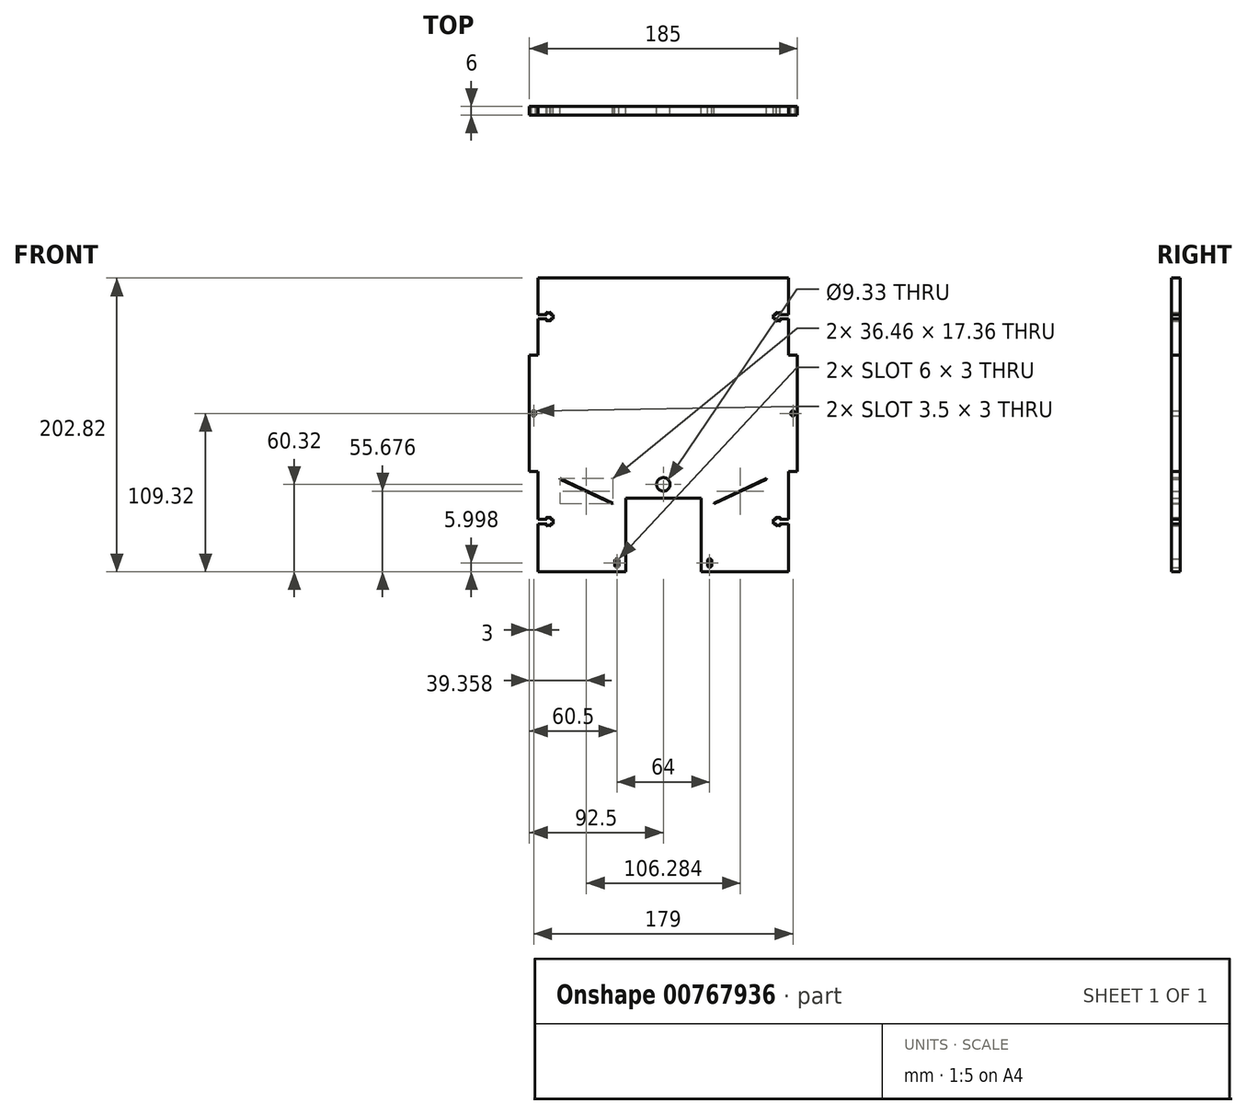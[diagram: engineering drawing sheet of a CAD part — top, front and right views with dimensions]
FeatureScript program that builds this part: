
annotation { "Feature Type Name" : "Feature", "Feature Type Description" : "" }
export const myFeature = defineFeature(function(context is Context, id is Id, definition is map)
    precondition{}
    {
        {
            var Q0;
            Q0=qCreatedBy(makeId("Front.planeOp"),FACE);
            var sketch = newSketch(context, id + "F0", { "sketchPlane" : qUnion([Q0])});
            skLineSegment(sketch, "E0.top", {"start": v(13.5, 187) * mm, "end": v(186.5, 187) * mm});
            skLineSegment(sketch, "E1", {"start": v(186.5, 187) * mm, "end": v(186.5, 161.75) * mm});
            skLineSegment(sketch, "E2.MirrorCS", {"start": v(13.5, 187) * mm, "end": v(13.5, 161.75) * mm});
            skLineSegment(sketch, "E3", {"start": v(100, 187) * mm, "end": v(100, -11.94) * mm, "construction": true});
            skLineSegment(sketch, "E4", {"start": v(74, 0) * mm, "end": v(74, 35) * mm});
            skLineSegment(sketch, "E5", {"start": v(126, 0) * mm, "end": v(126, 35) * mm});
            skLineSegment(sketch, "E6", {"start": v(74, 35) * mm, "end": v(126, 35) * mm});
            skLineSegment(sketch, "E7", {"start": v(-16.45, 22) * mm, "end": v(92.36, 22) * mm, "construction": true});
            skLineSegment(sketch, "E8", {"start": v(80, 24.12) * mm, "end": v(13.5, 55.14) * mm, "construction": true});
            skLineSegment(sketch, "E9.0", {"start": v(80.22, 24.58) * mm, "end": v(13.71, 55.59) * mm, "construction": true});
            skLineSegment(sketch, "E10", {"start": v(46.96, 40.08) * mm, "end": v(46.75, 39.63) * mm, "construction": true});
            skLineSegment(sketch, "E11.0", {"start": v(28.84, 48.53) * mm, "end": v(28.63, 48.08) * mm});
            skLineSegment(sketch, "E12.0", {"start": v(65.09, 31.63) * mm, "end": v(64.88, 31.18) * mm});
            skLineSegment(sketch, "E13", {"start": v(65.09, 31.63) * mm, "end": v(28.84, 48.53) * mm});
            skLineSegment(sketch, "E14", {"start": v(28.63, 48.08) * mm, "end": v(64.88, 31.18) * mm});
            skLineSegment(sketch, "E15", {"start": v(80, 24.12) * mm, "end": v(80.22, 24.58) * mm, "construction": true});
            skLineSegment(sketch, "E16", {"start": v(13.5, 55.14) * mm, "end": v(13.71, 55.59) * mm, "construction": true});
            skLineSegment(sketch, "E17.MirrorCS", {"start": v(134.91, 31.63) * mm, "end": v(171.16, 48.53) * mm});
            skLineSegment(sketch, "E18.MirrorCS", {"start": v(171.37, 48.08) * mm, "end": v(135.12, 31.18) * mm});
            skLineSegment(sketch, "E19.MirrorCS", {"start": v(134.91, 31.63) * mm, "end": v(135.12, 31.18) * mm});
            skLineSegment(sketch, "E20.MirrorCS", {"start": v(171.16, 48.53) * mm, "end": v(171.37, 48.08) * mm});
            skCircle(sketch, "E21", {"center": v(100, 44.5) * mm, "radius": 4.67 * mm});
            skLineSegment(sketch, "E22", {"start": v(74, 0) * mm, "end": v(74, -15.82) * mm});
            skLineSegment(sketch, "E23", {"start": v(74, -15.82) * mm, "end": v(13.5, -15.82) * mm});
            skLineSegment(sketch, "E24.MirrorCS", {"start": v(126, -15.82) * mm, "end": v(186.5, -15.82) * mm});
            skLineSegment(sketch, "E25.MirrorCS", {"start": v(126, 0) * mm, "end": v(126, -15.82) * mm});
            skLineSegment(sketch, "E26.left", {"start": v(66.5, -8.32) * mm, "end": v(66.5, -11.32) * mm});
            skLineSegment(sketch, "E26.right", {"start": v(69.5, -8.32) * mm, "end": v(69.5, -11.32) * mm});
            skArc(sketch, "E27", {"start": v(69.5, -8.32) * mm, "mid": v(68, -6.82) * mm, "end": v(66.5, -8.32) * mm});
            skArc(sketch, "E28", {"start": v(66.5, -11.32) * mm, "mid": v(68, -12.82) * mm, "end": v(69.5, -11.32) * mm});
            skArc(sketch, "E29.MirrorCS", {"start": v(130.5, -8.32) * mm, "mid": v(132, -6.82) * mm, "end": v(133.5, -8.32) * mm});
            skLineSegment(sketch, "E30.MirrorCS", {"start": v(130.5, -8.32) * mm, "end": v(130.5, -11.32) * mm});
            skLineSegment(sketch, "E31.MirrorCS", {"start": v(133.5, -8.32) * mm, "end": v(133.5, -11.32) * mm});
            skArc(sketch, "E32.MirrorCS", {"start": v(133.5, -11.32) * mm, "mid": v(132, -12.82) * mm, "end": v(130.5, -11.32) * mm});
            skLineSegment(sketch, "E33", {"start": v(7.5, 133.5) * mm, "end": v(7.5, 53.5) * mm});
            skLineSegment(sketch, "E34.MirrorCS", {"start": v(192.5, 133.5) * mm, "end": v(192.5, 53.5) * mm});
            skPoint(sketch, "E35", {"position": v(13.5, 160.25) * mm});
            skPoint(sketch, "E36", {"position": v(186.5, 160.25) * mm});
            skLineSegment(sketch, "E37", {"start": v(13.5, 53.4) * mm, "end": v(13.5, 20.34) * mm});
            skLineSegment(sketch, "E38", {"start": v(186.5, 53.4) * mm, "end": v(186.5, 20.34) * mm});
            skPoint(sketch, "E39", {"position": v(13.5, 18.84) * mm});
            skPoint(sketch, "E40", {"position": v(186.5, 18.84) * mm});
            skLineSegment(sketch, "E41.bottom", {"start": v(19.2, 158.75) * mm, "end": v(13.5, 158.75) * mm});
            skLineSegment(sketch, "E41.top", {"start": v(19.2, 161.75) * mm, "end": v(13.5, 161.75) * mm});
            skLineSegment(sketch, "E42", {"start": v(19.5, 158.45) * mm, "end": v(19.5, 157.7) * mm});
            skLineSegment(sketch, "E43", {"start": v(19.7, 157.5) * mm, "end": v(21.8, 157.5) * mm});
            skLineSegment(sketch, "E44", {"start": v(22, 157.7) * mm, "end": v(22, 158.45) * mm});
            skLineSegment(sketch, "E45.MirrorCS", {"start": v(19.5, 162.05) * mm, "end": v(19.5, 162.8) * mm});
            skLineSegment(sketch, "E46.MirrorCS", {"start": v(19.7, 163) * mm, "end": v(21.8, 163) * mm});
            skLineSegment(sketch, "E47.MirrorCS", {"start": v(22, 162.8) * mm, "end": v(22, 162.05) * mm});
            skPoint(sketch, "E48.visualSharp", {"position": v(19.5, 161.75) * mm});
            skArc(sketch, "E48.filletArc", {"start": v(19.2, 161.75) * mm, "mid": v(19.41, 161.84) * mm, "end": v(19.5, 162.05) * mm});
            skPoint(sketch, "E49.visualSharp", {"position": v(19.5, 158.75) * mm});
            skArc(sketch, "E49.filletArc", {"start": v(19.5, 158.45) * mm, "mid": v(19.41, 158.66) * mm, "end": v(19.2, 158.75) * mm});
            skPoint(sketch, "E50.visualSharp", {"position": v(22, 158.75) * mm});
            skArc(sketch, "E50.filletArc", {"start": v(22.3, 158.75) * mm, "mid": v(22.09, 158.66) * mm, "end": v(22, 158.45) * mm});
            skPoint(sketch, "E51.visualSharp", {"position": v(22, 161.75) * mm});
            skArc(sketch, "E51.filletArc", {"start": v(22, 162.05) * mm, "mid": v(22.09, 161.84) * mm, "end": v(22.3, 161.75) * mm});
            skArc(sketch, "E52", {"start": v(19.7, 157.5) * mm, "mid": v(19.36, 157.36) * mm, "end": v(19.5, 157.7) * mm});
            skArc(sketch, "E53", {"start": v(21.8, 157.5) * mm, "mid": v(22.14, 157.36) * mm, "end": v(22, 157.7) * mm});
            skArc(sketch, "E54", {"start": v(22, 162.8) * mm, "mid": v(22.14, 163.14) * mm, "end": v(21.8, 163) * mm});
            skArc(sketch, "E55", {"start": v(19.5, 162.8) * mm, "mid": v(19.36, 163.14) * mm, "end": v(19.7, 163) * mm});
            skLineSegment(sketch, "E56", {"start": v(24, 158.75) * mm, "end": v(24, 161.75) * mm});
            skLineSegment(sketch, "E57", {"start": v(24, 158.75) * mm, "end": v(22.3, 158.75) * mm});
            skLineSegment(sketch, "E58", {"start": v(24, 161.75) * mm, "end": v(22.3, 161.75) * mm});
            skLineSegment(sketch, "E59.bottom", {"start": v(19.2, 17.34) * mm, "end": v(13.5, 17.34) * mm});
            skLineSegment(sketch, "E59.top", {"start": v(19.2, 20.34) * mm, "end": v(13.5, 20.34) * mm});
            skLineSegment(sketch, "E60", {"start": v(19.5, 17.04) * mm, "end": v(19.5, 16.29) * mm});
            skLineSegment(sketch, "E61", {"start": v(19.7, 16.09) * mm, "end": v(21.8, 16.09) * mm});
            skLineSegment(sketch, "E62", {"start": v(22, 16.29) * mm, "end": v(22, 17.04) * mm});
            skLineSegment(sketch, "E63.MirrorCS", {"start": v(19.5, 20.64) * mm, "end": v(19.5, 21.39) * mm});
            skLineSegment(sketch, "E64.MirrorCS", {"start": v(19.7, 21.59) * mm, "end": v(21.8, 21.59) * mm});
            skLineSegment(sketch, "E65.MirrorCS", {"start": v(22, 21.39) * mm, "end": v(22, 20.64) * mm});
            skPoint(sketch, "E66.visualSharp", {"position": v(19.5, 20.34) * mm});
            skArc(sketch, "E66.filletArc", {"start": v(19.2, 20.34) * mm, "mid": v(19.41, 20.43) * mm, "end": v(19.5, 20.64) * mm});
            skPoint(sketch, "E67.visualSharp", {"position": v(19.5, 17.34) * mm});
            skArc(sketch, "E67.filletArc", {"start": v(19.5, 17.04) * mm, "mid": v(19.41, 17.25) * mm, "end": v(19.2, 17.34) * mm});
            skPoint(sketch, "E68.visualSharp", {"position": v(22, 17.34) * mm});
            skArc(sketch, "E68.filletArc", {"start": v(22.3, 17.34) * mm, "mid": v(22.09, 17.25) * mm, "end": v(22, 17.04) * mm});
            skPoint(sketch, "E69.visualSharp", {"position": v(22, 20.34) * mm});
            skArc(sketch, "E69.filletArc", {"start": v(22, 20.64) * mm, "mid": v(22.09, 20.43) * mm, "end": v(22.3, 20.34) * mm});
            skArc(sketch, "E70", {"start": v(19.7, 16.09) * mm, "mid": v(19.36, 15.95) * mm, "end": v(19.5, 16.29) * mm});
            skArc(sketch, "E71", {"start": v(21.8, 16.09) * mm, "mid": v(22.14, 15.95) * mm, "end": v(22, 16.29) * mm});
            skArc(sketch, "E72", {"start": v(22, 21.39) * mm, "mid": v(22.14, 21.73) * mm, "end": v(21.8, 21.59) * mm});
            skArc(sketch, "E73", {"start": v(19.5, 21.39) * mm, "mid": v(19.36, 21.73) * mm, "end": v(19.7, 21.59) * mm});
            skLineSegment(sketch, "E74", {"start": v(24, 17.34) * mm, "end": v(24, 20.34) * mm});
            skLineSegment(sketch, "E75", {"start": v(24, 17.34) * mm, "end": v(22.3, 17.34) * mm});
            skLineSegment(sketch, "E76", {"start": v(24, 20.34) * mm, "end": v(22.3, 20.34) * mm});
            skLineSegment(sketch, "E77.bottom", {"start": v(180.8, 161.75) * mm, "end": v(186.5, 161.75) * mm});
            skLineSegment(sketch, "E77.top", {"start": v(180.8, 158.75) * mm, "end": v(186.5, 158.75) * mm});
            skLineSegment(sketch, "E78", {"start": v(180.5, 162.05) * mm, "end": v(180.5, 162.8) * mm});
            skLineSegment(sketch, "E79", {"start": v(180.3, 163) * mm, "end": v(178.2, 163) * mm});
            skLineSegment(sketch, "E80", {"start": v(178, 162.8) * mm, "end": v(178, 162.05) * mm});
            skLineSegment(sketch, "E81.MirrorCS", {"start": v(180.5, 158.45) * mm, "end": v(180.5, 157.7) * mm});
            skLineSegment(sketch, "E82.MirrorCS", {"start": v(180.3, 157.5) * mm, "end": v(178.2, 157.5) * mm});
            skLineSegment(sketch, "E83.MirrorCS", {"start": v(178, 157.7) * mm, "end": v(178, 158.45) * mm});
            skPoint(sketch, "E84.visualSharp", {"position": v(180.5, 158.75) * mm});
            skArc(sketch, "E84.filletArc", {"start": v(180.8, 158.75) * mm, "mid": v(180.59, 158.66) * mm, "end": v(180.5, 158.45) * mm});
            skPoint(sketch, "E85.visualSharp", {"position": v(180.5, 161.75) * mm});
            skArc(sketch, "E85.filletArc", {"start": v(180.5, 162.05) * mm, "mid": v(180.59, 161.84) * mm, "end": v(180.8, 161.75) * mm});
            skPoint(sketch, "E86.visualSharp", {"position": v(178, 161.75) * mm});
            skArc(sketch, "E86.filletArc", {"start": v(177.7, 161.75) * mm, "mid": v(177.91, 161.84) * mm, "end": v(178, 162.05) * mm});
            skPoint(sketch, "E87.visualSharp", {"position": v(178, 158.75) * mm});
            skArc(sketch, "E87.filletArc", {"start": v(178, 158.45) * mm, "mid": v(177.91, 158.66) * mm, "end": v(177.7, 158.75) * mm});
            skArc(sketch, "E88", {"start": v(180.3, 163) * mm, "mid": v(180.64, 163.14) * mm, "end": v(180.5, 162.8) * mm});
            skArc(sketch, "E89", {"start": v(178.2, 163) * mm, "mid": v(177.86, 163.14) * mm, "end": v(178, 162.8) * mm});
            skArc(sketch, "E90", {"start": v(178, 157.7) * mm, "mid": v(177.86, 157.36) * mm, "end": v(178.2, 157.5) * mm});
            skArc(sketch, "E91", {"start": v(180.5, 157.7) * mm, "mid": v(180.64, 157.36) * mm, "end": v(180.3, 157.5) * mm});
            skLineSegment(sketch, "E92", {"start": v(176, 161.75) * mm, "end": v(176, 158.75) * mm});
            skLineSegment(sketch, "E93", {"start": v(176, 161.75) * mm, "end": v(177.7, 161.75) * mm});
            skLineSegment(sketch, "E94", {"start": v(176, 158.75) * mm, "end": v(177.7, 158.75) * mm});
            skLineSegment(sketch, "E95.bottom", {"start": v(180.8, 20.34) * mm, "end": v(186.5, 20.34) * mm});
            skLineSegment(sketch, "E95.top", {"start": v(180.8, 17.34) * mm, "end": v(186.5, 17.34) * mm});
            skLineSegment(sketch, "E96", {"start": v(180.5, 20.64) * mm, "end": v(180.5, 21.39) * mm});
            skLineSegment(sketch, "E97", {"start": v(180.3, 21.59) * mm, "end": v(178.2, 21.59) * mm});
            skLineSegment(sketch, "E98", {"start": v(178, 21.39) * mm, "end": v(178, 20.64) * mm});
            skLineSegment(sketch, "E99.MirrorCS", {"start": v(180.5, 17.04) * mm, "end": v(180.5, 16.29) * mm});
            skLineSegment(sketch, "E100.MirrorCS", {"start": v(180.3, 16.09) * mm, "end": v(178.2, 16.09) * mm});
            skLineSegment(sketch, "E101.MirrorCS", {"start": v(178, 16.29) * mm, "end": v(178, 17.04) * mm});
            skPoint(sketch, "E102.visualSharp", {"position": v(180.5, 17.34) * mm});
            skArc(sketch, "E102.filletArc", {"start": v(180.8, 17.34) * mm, "mid": v(180.59, 17.25) * mm, "end": v(180.5, 17.04) * mm});
            skPoint(sketch, "E103.visualSharp", {"position": v(180.5, 20.34) * mm});
            skArc(sketch, "E103.filletArc", {"start": v(180.5, 20.64) * mm, "mid": v(180.59, 20.43) * mm, "end": v(180.8, 20.34) * mm});
            skPoint(sketch, "E104.visualSharp", {"position": v(178, 20.34) * mm});
            skArc(sketch, "E104.filletArc", {"start": v(177.7, 20.34) * mm, "mid": v(177.91, 20.43) * mm, "end": v(178, 20.64) * mm});
            skPoint(sketch, "E105.visualSharp", {"position": v(178, 17.34) * mm});
            skArc(sketch, "E105.filletArc", {"start": v(178, 17.04) * mm, "mid": v(177.91, 17.25) * mm, "end": v(177.7, 17.34) * mm});
            skArc(sketch, "E106", {"start": v(180.3, 21.59) * mm, "mid": v(180.64, 21.73) * mm, "end": v(180.5, 21.39) * mm});
            skArc(sketch, "E107", {"start": v(178.2, 21.59) * mm, "mid": v(177.86, 21.73) * mm, "end": v(178, 21.39) * mm});
            skArc(sketch, "E108", {"start": v(178, 16.29) * mm, "mid": v(177.86, 15.95) * mm, "end": v(178.2, 16.09) * mm});
            skArc(sketch, "E109", {"start": v(180.5, 16.29) * mm, "mid": v(180.64, 15.95) * mm, "end": v(180.3, 16.09) * mm});
            skLineSegment(sketch, "E110", {"start": v(176, 20.34) * mm, "end": v(176, 17.34) * mm});
            skLineSegment(sketch, "E111", {"start": v(176, 20.34) * mm, "end": v(177.7, 20.34) * mm});
            skLineSegment(sketch, "E112", {"start": v(176, 17.34) * mm, "end": v(177.7, 17.34) * mm});
            skLineSegment(sketch, "E113.trimOffspring", {"start": v(186.5, 17.34) * mm, "end": v(186.5, -15.82) * mm});
            skLineSegment(sketch, "E114.trimOffspring", {"start": v(13.5, 17.34) * mm, "end": v(13.5, -15.82) * mm});
            skLineSegment(sketch, "E115.trimOffspring", {"start": v(13.5, 158.75) * mm, "end": v(13.5, 133.6) * mm});
            skLineSegment(sketch, "E116.trimOffspring", {"start": v(186.5, 158.75) * mm, "end": v(186.5, 133.6) * mm});
            skLineSegment(sketch, "E117", {"start": v(7.5, 133.5) * mm, "end": v(7.5, 133.6) * mm});
            skLineSegment(sketch, "E118", {"start": v(7.5, 133.6) * mm, "end": v(13.5, 133.6) * mm});
            skLineSegment(sketch, "E119.MirrorCS", {"start": v(192.5, 133.6) * mm, "end": v(186.5, 133.6) * mm});
            skLineSegment(sketch, "E120.MirrorCS", {"start": v(192.5, 133.5) * mm, "end": v(192.5, 133.6) * mm});
            skPoint(sketch, "E121.MirrorCS.end.orphan", {"position": v(192.5, 133.5) * mm});
            skPoint(sketch, "E121.MirrorCS.start.orphan", {"position": v(186.5, 133.5) * mm});
            skLineSegment(sketch, "E122", {"start": v(192.5, 53.5) * mm, "end": v(192.5, 53.4) * mm});
            skLineSegment(sketch, "E123", {"start": v(192.5, 53.4) * mm, "end": v(186.5, 53.4) * mm});
            skPoint(sketch, "E124.MirrorCS.end.orphan", {"position": v(186.5, 53.5) * mm});
            skPoint(sketch, "E124.MirrorCS.start.orphan", {"position": v(192.5, 53.5) * mm});
            skLineSegment(sketch, "E125.MirrorCS", {"start": v(7.5, 53.4) * mm, "end": v(13.5, 53.4) * mm});
            skLineSegment(sketch, "E126.MirrorCS", {"start": v(7.5, 53.5) * mm, "end": v(7.5, 53.4) * mm});
            skPoint(sketch, "E127.orphan", {"position": v(13.5, 53.5) * mm});
            skPoint(sketch, "E128", {"position": v(10.5, 93.5) * mm});
            skPoint(sketch, "E128.positionSnap0", {"position": v(7.5, 93.5) * mm});
            skArc(sketch, "E129", {"start": v(12, 93.75) * mm, "mid": v(10.5, 95.25) * mm, "end": v(9, 93.75) * mm});
            skArc(sketch, "E130", {"start": v(9, 93.25) * mm, "mid": v(10.5, 91.75) * mm, "end": v(12, 93.25) * mm});
            skLineSegment(sketch, "E131", {"start": v(9, 93.25) * mm, "end": v(9, 93.75) * mm});
            skLineSegment(sketch, "E132", {"start": v(12, 93.25) * mm, "end": v(12, 93.75) * mm});
            skPoint(sketch, "E133.positionSnap0", {"position": v(9, 93.5) * mm});
            skArc(sketch, "E134.MirrorCS", {"start": v(191, 93.25) * mm, "mid": v(189.5, 91.75) * mm, "end": v(188, 93.25) * mm});
            skArc(sketch, "E135.MirrorCS", {"start": v(188, 93.75) * mm, "mid": v(189.5, 95.25) * mm, "end": v(191, 93.75) * mm});
            skLineSegment(sketch, "E136.MirrorCS", {"start": v(188, 93.25) * mm, "end": v(188, 93.75) * mm});
            skLineSegment(sketch, "E137.MirrorCS", {"start": v(191, 93.25) * mm, "end": v(191, 93.75) * mm});
            skSolve(sketch);
        }
        {
            var Q0;
            Q0=makeQuery(id+"F0.imprint","IMPRINT",FACE,{"disambiguationData":[TD([[makeQuery(id+"F0.imprint","IMPRINT",EDGE,{"derivedFrom":sQuery(id+"F0.wireOp",EDGE,"E0.top")}),-1.0]])]});
            extrude(context, id + "F1", {"entities" : qUnion([Q0]), "depth" : 6 * mm, "offsetDistance" : 25 * mm});
        }
    });
